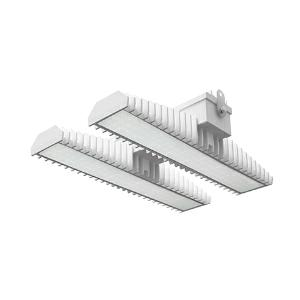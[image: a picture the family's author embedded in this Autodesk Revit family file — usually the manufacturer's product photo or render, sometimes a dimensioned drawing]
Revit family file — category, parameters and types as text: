
# Revit family: 3f_filippi_-_3f_lem_concentrato_3f_filippi_-_58906_a0812_-_3f_lem_2_led_100_dali_cr_conc___vs_2a61
name_source: partatom
category: Lighting Fixtures
units: mm (PartAtom-declared; Revit-internal decimal feet)

## family parameters
Cut with Voids When Loaded = No
Host = Face
Light Source = No
Part Type = Normal
Room Calculation Point = No
Round Connector Dimension = Use Diameter
Shared = No

## types (1)
- 3F Filippi - 3F LEM Concentrato (1 x LED, 13214 lm, 109 W, 4000 K)
    Apparent Load = 109 VA
    Approval mark = CE
    CIE Flux Codes = 78 93 98 100 100
    Color Rendering = 80
    Color Temperature = 4000 K
    Control Gear = Electronic transformer
    Default Elevation = 1800 mm
    Description = Industrial luminaire with high light output and high luminous efficiency designed with the most innovative technologies for environments with temperature up to 55°C.

ILLUMINOTECHNICAL
Luminous efficiency 100% (DLOR 98%, ULOR 2%).
Initial luminous flux of the luminaire 13214 lm.
Direct symmetric narrow distribution: the illuminated area has a elliptical shape.
Installation Interdistance Transv.D = 0.60 x hu - Long.D = 0.91 x hu.
Tabular UGR (CIE 117 - 4H-8H; S=0.25H; 70/50/20): RUG 19.5 - 21.
Beam angle: 38° - 61°.
Luminous efficacy 121 lm/W.
Lifetime (L93/B10): 30000 h. (tq+25°C)
Lifetime (L90/B10): 50000 h. (tq+25°C)
Lifetime (L85/B10): 80000 h. (tq+25°C)
Lifetime (L80/B10): 100000 h. (tq+25°C)
Lifetime (L85/B10): 50000 h. (tq+55°C)
Sudden decreased luminous flux after 50000 hours: 0% (C0).
Photobiological safety in compliance with IEC/TR 62778: RG0 risk exempt, (IEC 62471).
In compliance with IEC/EN 62722-2-1 - IEC/EN 62717 standards.

SOURCE
2 Mid-Power linear LED modules 50W/840.
Energy efficiency class (UE 2019/2020 - UE 2019/2015): C.
CIE 13.3 Colour rendering index: CRI >80 (R9 <50%).
IES TM-30 Fidelity Index: Rf = 84 Rg = 95.
CCT nominal colour temperature 4000 K.
Colour initial tolerance (MacAdam): SDCM 3.

MECHANICAL
Passive modular heatsinks in die-casted aluminium, painted in white colour.
To optimize the thermal management of the LED module, the heatsinks are oversized and provided with self-cleaning of cooling fins.
Wiring body in aluminium and galvanised steel anchored solidly to the sinks and thermally separated.
3F Lens lenses with high luminous efficiency, transparent methacrylate (PMMA), fixed to the LED modules.
Fixing brackets in stainless steel.
Luminaire with limited surface temperature. - D - (EN 60598-2-24)
Dimensions: 470x542 mm, height 133 mm. Weight 10.105 kg.
IP65 protection degree.
Mechanical strength to impacts IK06 (1 joule).
Glow-wire test resistance 650°C.

ELECTRICAL
Halogen Free DALI-2 DATI (Parts 251, 252, 253), PUSH-DIM, electronic wiring 230V-50/60Hz, power factor 0.97 at full load, THD <25%, constant output current, class I, 1 driver, 1 DALI addresse.
Power of the luminaire 109 W.
ENEC - CE.
Flicker: <4%.
Luminaire compliant with EN 60598-2-22 for power supply from a centralised emergency system CPSS (Central Power Supply System), not incorporated in the luminaire - high risk areas excluded. The default power and flux are 100% in AC and 15% in DC.
Ambient temperature from -30°C to +55°C.
Temperature class T6 max 85°C.
Quick connection via M25 5P connector with 9-13 mm tightening range.
Power unit positioned on a separate compartment by the LED module to ensure optimum temperatures of cabling components, to be inspectable and maintainable.
Relative humidity UR: <85%.

INSTALLATION
Ceiling / Suspended / Wall.
All accessories dedicated to this product are available on the Catalog and on our website www.3F-Filippi.com.

ACCESSORIES
A0812 - Anti-glare microprismatic VS moulded glass, tempered, not flammable, with sealing gasket.
One required for each light module. The pack contains 10 pieces.

APPLICATIONS
In commercial environments, exhibition and industrial areas, stores, open areas.
Applications with high ambient temperature up to 55°C.
Environments in which it is necessary a total protection against falling fragments (eg environments with foodstuffs or machines with moving parts or with extreme temperature changes), use luminaires with polycarbonate lenses.

LIGHT MANAGEMENT
Recommended minimum setting: 10%.
The luminaire, equipped with (DALI-2 DATI) driver, can be controlled manually with 3F Easy Dim technology or automatically/manually with wired or wireless DALI/D2D control systems.
The D2D driver guarantees interoperability with other devices with the same certification by making the following information available:
Device Data (Part 251), Energy Report (Part 252), Diagnosis & Maintenance (Part 253).
In electrical systems without a regulation system (manual or automatic) and DALI bus, a suitable jumper must be made on the DA-DA terminals of the appliance.

WARNING
Fixture not suitable for cold stores with an ambient temperature <0°C and/or relative humidity >85%.
Luminaire designed for disposal/recycling at end-of-life.
Replaceable (LED only) light source by a professional. Replaceable control gear by a professional.
    Height = 133 mm  [stored 0.436352 ft]
    Lamp = 1 x LED
    Lamp Light Flux = 13214 lm
    Lamp Power = 109 W
    Lamp count = 1
    Length = 470 mm
    Lifetime = 50000 h
    Luminous efficacy = 121 lm/W
    Manufacturer = 3F Filippi
    ModVariant = No
    Model = 3F Filippi - 58906+A0812 - 3F LEM 2 LED 100 DALI CR CONC + VS
    Mounting Place = Ceiling
    Mounting Type = Pendant
    Number of Poles = 1
    OnlyDefault = Yes
    Power Factor = 1
    Product Name = 3F Filippi - 3F LEM Concentrato
    Product group = pendant luminaire
    ProductGroupID = 9
    Protection Class = Protection class I
    Protection Degree = IP 65
    RLX_Detail_Level = 1
    RLX_Emergency_Light_Flux = 0 lm
    RLX_Emergency_Type = 0
    RLX_Emergency_Type_DB = No
    RlxData = <blob elided: 97885 chars, md5=e101ac22>
    Socket = socket
    Standby Power = 0 W
    System Light Flux = 13214 lm
    System Power = 109 W
    Type Comments = Product without accessories
    Type Image = 3f_filippi_-_lem_2__a0812.jpg
    URL = http://relux.com
    VarID = ---
    Voltage = 0 V
    Weight = 0.00 kg
    Width = 542 mm

note: [stored X ft] marks values corroborated as IEEE doubles in the binary element streams (Revit-internal decimal feet)

## geometry (parser evidence)
native form markers: Blend x4, Sweep x13
no freeform markers — native parametric forms only
